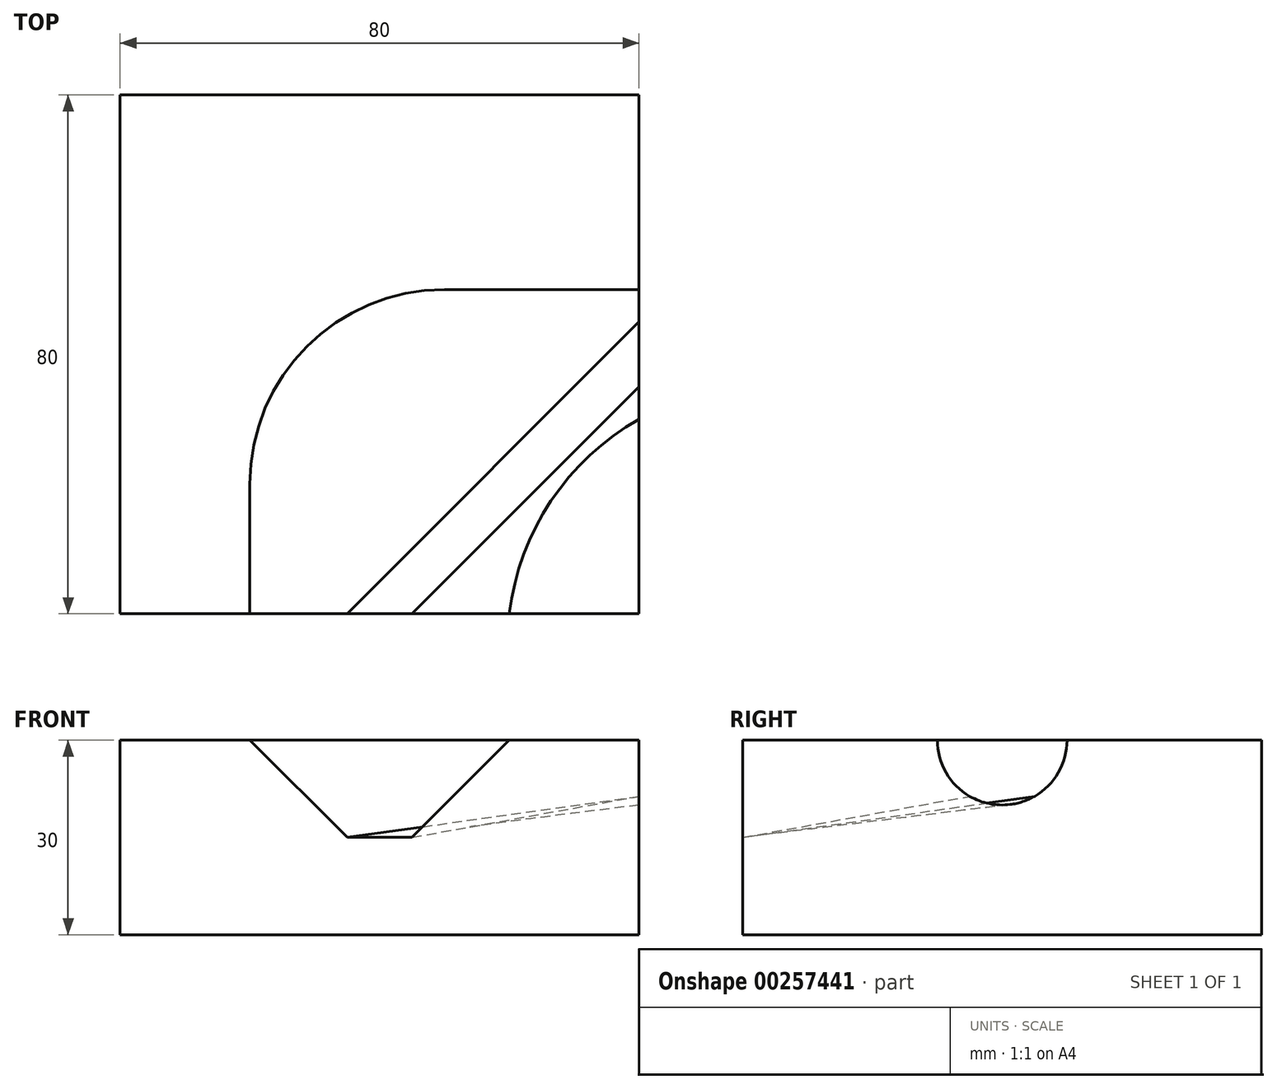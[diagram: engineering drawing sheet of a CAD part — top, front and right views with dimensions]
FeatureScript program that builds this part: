
annotation { "Feature Type Name" : "Feature", "Feature Type Description" : "" }
export const myFeature = defineFeature(function(context is Context, id is Id, definition is map)
    precondition{}
    {
        {
            var Q0;
            Q0=qCreatedBy(makeId("Top.planeOp"),FACE);
            var sketch = newSketch(context, id + "F0", { "sketchPlane" : qUnion([Q0])});
            skLineSegment(sketch, "E0.bottom", {"start": v(-40, -40) * mm, "end": v(40, -40) * mm});
            skLineSegment(sketch, "E0.top", {"start": v(-40, 40) * mm, "end": v(40, 40) * mm});
            skLineSegment(sketch, "E0.left", {"start": v(-40, -40) * mm, "end": v(-40, 40) * mm});
            skLineSegment(sketch, "E0.right", {"start": v(40, -40) * mm, "end": v(40, 40) * mm});
            skPoint(sketch, "E0.middle", {"position": v(0, 0) * mm});
            skSolve(sketch);
        }
        {
            var Q0;
            Q0=makeQuery(id+"F0.imprint","IMPRINT",FACE,{"disambiguationData":[TD([[makeQuery(id+"F0.imprint","IMPRINT",EDGE,{"derivedFrom":sQuery(id+"F0.wireOp",EDGE,"E0.bottom")}),1.0]])]});
            extrude(context, id + "F1", {"entities" : qUnion([Q0]), "endBound" : BoundingType.SYMMETRIC, "depth" : 30 * mm});
        }
        {
            var Q0;
            Q0=makeQuery(id+"F1.opExtrude","SWEPT_FACE",FACE,{"disambiguationData":[OSD([sQuery(id+"F0.wireOp",EDGE,"E0.bottom")])]});
            var sketch = newSketch(context, id + "F2", { "sketchPlane" : qUnion([Q0])});
            skLineSegment(sketch, "E1", {"start": v(-20, 15) * mm, "end": v(-5, 0) * mm});
            skLineSegment(sketch, "E2", {"start": v(-5, 0) * mm, "end": v(5, 0) * mm});
            skLineSegment(sketch, "E3", {"start": v(5, 0) * mm, "end": v(20, 15) * mm});
            skLineSegment(sketch, "E4.0.0", {"start": v(-40, -15) * mm, "end": v(40, -15) * mm, "construction": true});
            skLineSegment(sketch, "E4.0.1", {"start": v(40, -15) * mm, "end": v(40, 15) * mm, "construction": true});
            skLineSegment(sketch, "E4.0.2", {"start": v(40, 15) * mm, "end": v(-40, 15) * mm, "construction": true});
            skLineSegment(sketch, "E4.0.3", {"start": v(-40, 15) * mm, "end": v(-40, -15) * mm, "construction": true});
            skSolve(sketch);
        }
        {
            var Q0;
            Q0=makeQuery(id+"F1.opExtrude","SWEPT_FACE",FACE,{"disambiguationData":[OSD([sQuery(id+"F0.wireOp",EDGE,"E0.right")])]});
            var sketch = newSketch(context, id + "F3", { "sketchPlane" : qUnion([Q0])});
            skLineSegment(sketch, "E5.0.0", {"start": v(-40, -15) * mm, "end": v(40, -15) * mm, "construction": true});
            skLineSegment(sketch, "E5.0.1", {"start": v(40, -15) * mm, "end": v(40, 15) * mm, "construction": true});
            skLineSegment(sketch, "E5.0.2", {"start": v(40, 15) * mm, "end": v(-40, 15) * mm, "construction": true});
            skLineSegment(sketch, "E5.0.3", {"start": v(-40, 15) * mm, "end": v(-40, -15) * mm, "construction": true});
            skArc(sketch, "E6", {"start": v(-10, 15) * mm, "mid": v(0, 5) * mm, "end": v(10, 15) * mm});
            skSolve(sketch);
        }
        {
            var Q0;
            Q0=makeQuery(id+"F1.opExtrude","CAP_FACE",FACE,{"disambiguationData":[OSD([sQuery(id+"F0.wireOp",EDGE,"E0.bottom"),sQuery(id+"F0.wireOp",EDGE,"E0.top"),sQuery(id+"F0.wireOp",EDGE,"E0.left"),sQuery(id+"F0.wireOp",EDGE,"E0.right")])],"isStart":false});
            var sketch = newSketch(context, id + "F4", { "sketchPlane" : qUnion([Q0])});
            skPoint(sketch, "E7.0", {"position": v(40, 10) * mm});
            skPoint(sketch, "E8.0", {"position": v(40, -10) * mm});
            skPoint(sketch, "E9.0", {"position": v(-20, -40) * mm});
            skPoint(sketch, "E10.0", {"position": v(20, -40) * mm});
            skLineSegment(sketch, "E11", {"start": v(40, -40) * mm, "end": v(71.47, -40) * mm, "construction": true});
            skArc(sketch, "E12", {"start": v(40, -10) * mm, "mid": v(26.43, -22.62) * mm, "end": v(20, -40) * mm});
            skLineSegment(sketch, "E13", {"start": v(-20, -40) * mm, "end": v(-20, -20) * mm});
            skArc(sketch, "E14", {"start": v(-20, -20) * mm, "mid": v(-11.21, 1.21) * mm, "end": v(10, 10) * mm});
            skLineSegment(sketch, "E15", {"start": v(10, 10) * mm, "end": v(40, 10) * mm});
            skSolve(sketch);
        }
        {
            var Q0;
            {var subQ2=sQuery(id+"F4.wireOp",EDGE,"E12");Q0=makeQuery(id+"F4.imprint","IMPRINT",FACE,{"disambiguationData":[TD([[makeQuery(id+"F4.imprint","IMPRINT",EDGE,{"derivedFrom":subQ2}),-1.0]])]});}
            var sketch = newSketch(context, id + "F5", { "sketchPlane" : qUnion([Q0])});
            skLineSegment(sketch, "E16.0", {"start": v(-20, -40) * mm, "end": v(-20, -20) * mm});
            skArc(sketch, "E17.0", {"start": v(-20, -20) * mm, "mid": v(-11.21, 1.21) * mm, "end": v(10, 10) * mm});
            skLineSegment(sketch, "E18.0", {"start": v(10, 10) * mm, "end": v(40, 10) * mm});
            skSolve(sketch);
        }
        {
            var Q1;
            {var subQ0=sQuery(id+"F2.wireOp",EDGE,"E1");Q1=makeQuery(id+"F2.imprint","IMPRINT",FACE,{"disambiguationData":[TD([[makeQuery(id+"F2.imprint","IMPRINT",EDGE,{"derivedFrom":subQ0}),1.0]])]});}
            var Q2;
            {var subQ0=sQuery(id+"F3.wireOp",EDGE,"E6");Q2=makeQuery(id+"F3.imprint","IMPRINT",FACE,{"disambiguationData":[TD([[makeQuery(id+"F3.imprint","IMPRINT",EDGE,{"derivedFrom":subQ0}),1.0]])]});}
            var Q3;
            Q3=sQuery(id+"F4.wireOp",EDGE,"E12");
            var Q4;
            Q4 = qConstructionFilter(qBodyType(qCreatedBy(id + "F5" ,EDGE), BodyType.WIRE), ConstructionObject.NO);
            loft(context, id + "F6", {"operationType" : NewBodyOperationType.REMOVE, "addGuides" : true, "sheetProfilesArray" : [{ "sheetProfileEntities" : qUnion([Q1]) }, { "sheetProfileEntities" : qUnion([Q2]) }], "guidesArray" : [{ "guideEntities" : qUnion([Q3]), "guideDerivativeType" : LoftGuideDerivativeType.DEFAULT, "guideDerivativeMagnitude" : 1 }, { "guideEntities" : qUnion([Q4]), "guideDerivativeType" : LoftGuideDerivativeType.DEFAULT, "guideDerivativeMagnitude" : 1 }]});
        }
    });
